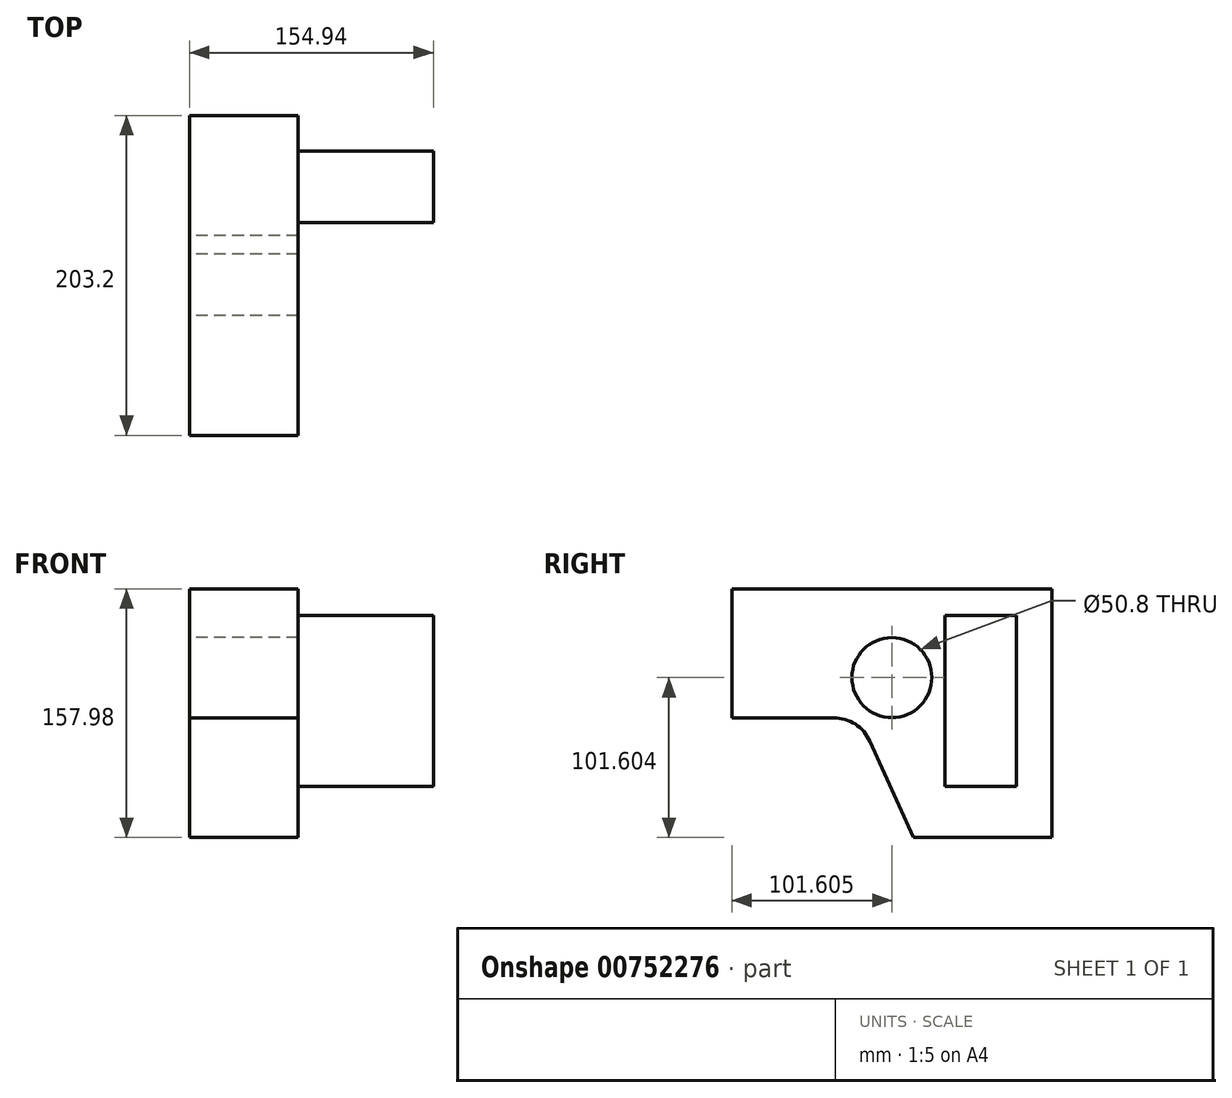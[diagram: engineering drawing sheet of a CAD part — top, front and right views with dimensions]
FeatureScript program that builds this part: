
annotation { "Feature Type Name" : "Feature", "Feature Type Description" : "" }
export const myFeature = defineFeature(function(context is Context, id is Id, definition is map)
    precondition{}
    {
        {
            var Q0;
            Q0=qCreatedBy(makeId("Right.planeOp"),FACE);
            var sketch = newSketch(context, id + "F0", { "sketchPlane" : qUnion([Q0])});
            skLineSegment(sketch, "E0", {"start": v(-70.74, -11.5) * mm, "end": v(-135.27, -11.5) * mm});
            skLineSegment(sketch, "E1", {"start": v(-135.27, -11.5) * mm, "end": v(-135.27, 70.43) * mm});
            skLineSegment(sketch, "E2", {"start": v(-135.27, 70.43) * mm, "end": v(67.93, 70.43) * mm});
            skLineSegment(sketch, "E3", {"start": v(67.93, 70.43) * mm, "end": v(67.93, -87.55) * mm});
            skLineSegment(sketch, "E4", {"start": v(67.93, -87.55) * mm, "end": v(-20.03, -87.55) * mm});
            skLineSegment(sketch, "E5", {"start": v(-20.03, -87.55) * mm, "end": v(-47.58, -26.45) * mm});
            skCircle(sketch, "E6", {"center": v(-33.67, 14.05) * mm, "radius": 25.4 * mm});
            skPoint(sketch, "E7.visualSharp", {"position": v(-54.33, -11.5) * mm});
            skArc(sketch, "E7.filletArc", {"start": v(-47.58, -26.45) * mm, "mid": v(-56.96, -15.56) * mm, "end": v(-70.74, -11.5) * mm});
            skSolve(sketch);
        }
        {
            var Q0;
            Q0=makeQuery(id+"F0.imprint","IMPRINT",FACE,{"disambiguationData":[TD([[makeQuery(id+"F0.imprint","IMPRINT",EDGE,{"derivedFrom":sQuery(id+"F0.wireOp",EDGE,"E0")}),-1.0]])]});
            extrude(context, id + "F1", {"entities" : qUnion([Q0]), "depth" : 69.1 * mm, "offsetDistance" : 25.4 * mm});
        }
        {
            var Q0;
            Q0=makeQuery(id+"F1.opExtrude","CAP_FACE",FACE,{"disambiguationData":[OSD([sQuery(id+"F0.wireOp",EDGE,"E0"),sQuery(id+"F0.wireOp",EDGE,"E1"),sQuery(id+"F0.wireOp",EDGE,"E2"),sQuery(id+"F0.wireOp",EDGE,"E3"),sQuery(id+"F0.wireOp",EDGE,"E4"),sQuery(id+"F0.wireOp",EDGE,"E5"),sQuery(id+"F0.wireOp",EDGE,"E6"),sQuery(id+"F0.wireOp",EDGE,"E7.filletArc")])],"isStart":false});
            var sketch = newSketch(context, id + "F2", { "sketchPlane" : qUnion([Q0])});
            skLineSegment(sketch, "E8.bottom", {"start": v(45.3, -54.93) * mm, "end": v(0, -54.93) * mm});
            skLineSegment(sketch, "E8.top", {"start": v(45.3, 53.53) * mm, "end": v(0, 53.53) * mm});
            skLineSegment(sketch, "E8.left", {"start": v(45.3, -54.93) * mm, "end": v(45.3, 53.53) * mm});
            skLineSegment(sketch, "E8.right", {"start": v(0, -54.93) * mm, "end": v(0, 53.53) * mm});
            skSolve(sketch);
        }
        {
            var Q0;
            Q0=makeQuery(id+"F2.imprint","IMPRINT",FACE,{"disambiguationData":[TD([[makeQuery(id+"F2.imprint","IMPRINT",EDGE,{"derivedFrom":sQuery(id+"F2.wireOp",EDGE,"E8.bottom")}),-1.0]])]});
            extrude(context, id + "F3", {"entities" : qUnion([Q0]), "depth" : 85.85 * mm, "offsetDistance" : 25.4 * mm});
        }
    });
